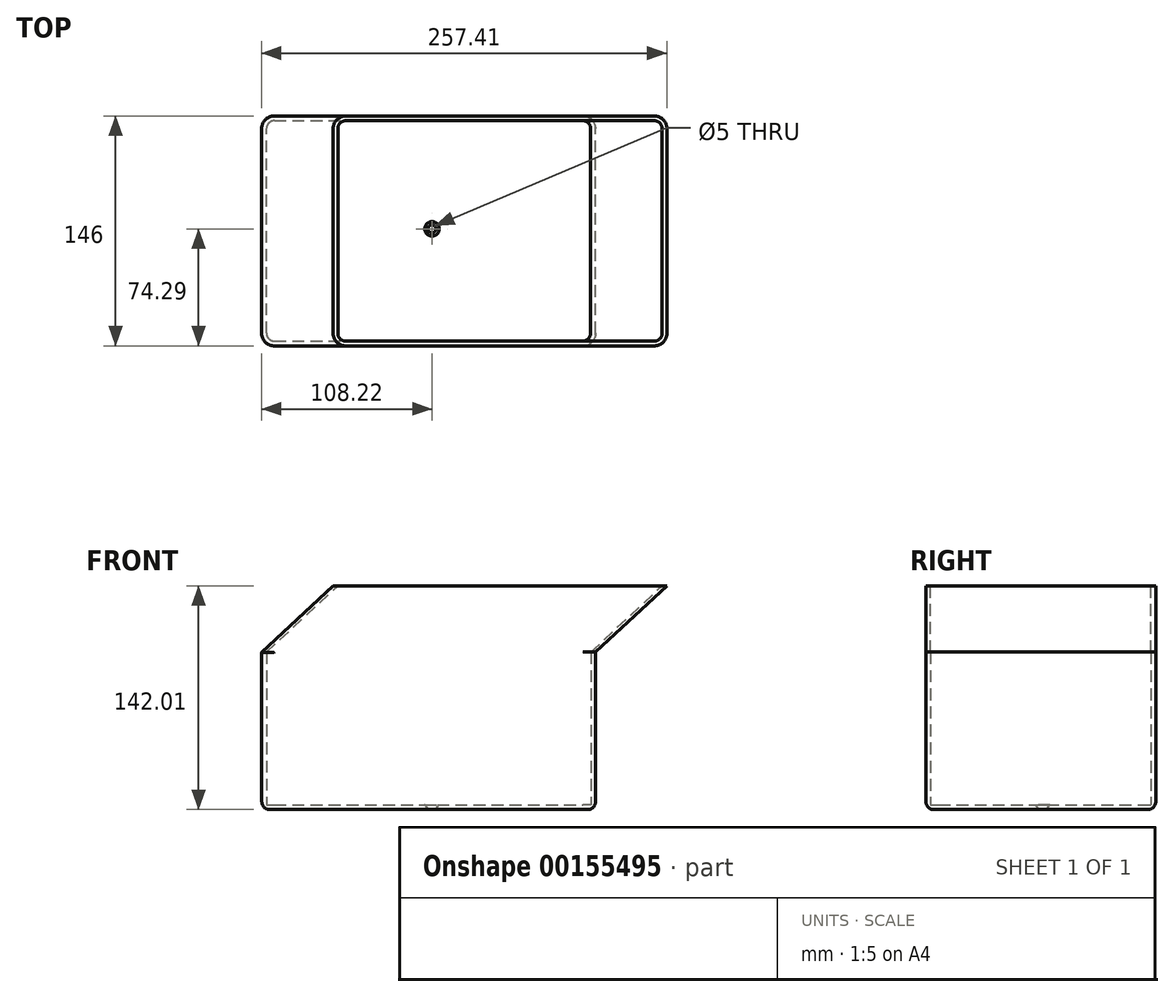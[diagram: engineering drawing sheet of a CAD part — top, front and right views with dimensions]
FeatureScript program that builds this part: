
annotation { "Feature Type Name" : "Feature", "Feature Type Description" : "" }
export const myFeature = defineFeature(function(context is Context, id is Id, definition is map)
    precondition{}
    {
        {
            var Q0;
            Q0=qCreatedBy(makeId("Top.planeOp"),FACE);
            var sketch = newSketch(context, id + "F0", { "sketchPlane" : qUnion([Q0])});
            skLineSegment(sketch, "E0.bottom", {"start": v(-100.1, -71.29) * mm, "end": v(95.9, -71.29) * mm});
            skLineSegment(sketch, "E0.top", {"start": v(-100.1, 68.71) * mm, "end": v(95.9, 68.71) * mm});
            skLineSegment(sketch, "E0.left", {"start": v(-105.1, -66.29) * mm, "end": v(-105.1, 63.71) * mm});
            skLineSegment(sketch, "E0.right", {"start": v(100.9, -66.29) * mm, "end": v(100.9, 63.71) * mm});
            skLineSegment(sketch, "E1.0", {"start": v(-100.1, 71.71) * mm, "end": v(95.9, 71.71) * mm});
            skLineSegment(sketch, "E1.1", {"start": v(-108.1, -66.29) * mm, "end": v(-108.1, 63.71) * mm});
            skLineSegment(sketch, "E1.2", {"start": v(-100.1, -74.29) * mm, "end": v(95.9, -74.29) * mm});
            skLineSegment(sketch, "E1.3", {"start": v(103.9, -66.29) * mm, "end": v(103.9, 63.71) * mm});
            skPoint(sketch, "E2.visualSharp", {"position": v(-105.1, 68.71) * mm});
            skArc(sketch, "E2.filletArc", {"start": v(-100.1, 68.71) * mm, "mid": v(-103.63, 67.25) * mm, "end": v(-105.1, 63.71) * mm});
            skPoint(sketch, "E3.visualSharp", {"position": v(100.9, 68.71) * mm});
            skArc(sketch, "E3.filletArc", {"start": v(100.9, 63.71) * mm, "mid": v(99.44, 67.25) * mm, "end": v(95.9, 68.71) * mm});
            skPoint(sketch, "E4.visualSharp", {"position": v(100.9, -71.29) * mm});
            skArc(sketch, "E4.filletArc", {"start": v(95.9, -71.29) * mm, "mid": v(99.44, -69.82) * mm, "end": v(100.9, -66.29) * mm});
            skArc(sketch, "E5.0", {"start": v(-100.1, 71.71) * mm, "mid": v(-105.75, 69.37) * mm, "end": v(-108.1, 63.71) * mm});
            skArc(sketch, "E6.0", {"start": v(103.9, 63.71) * mm, "mid": v(101.56, 69.37) * mm, "end": v(95.9, 71.71) * mm});
            skArc(sketch, "E7.0", {"start": v(95.9, -74.29) * mm, "mid": v(101.56, -71.94) * mm, "end": v(103.9, -66.29) * mm});
            skPoint(sketch, "E8.visualSharp", {"position": v(-105.1, -71.29) * mm});
            skArc(sketch, "E8.filletArc", {"start": v(-105.1, -66.29) * mm, "mid": v(-103.63, -69.82) * mm, "end": v(-100.1, -71.29) * mm});
            skArc(sketch, "E9.0", {"start": v(-108.1, -66.29) * mm, "mid": v(-105.75, -71.94) * mm, "end": v(-100.1, -74.29) * mm});
            skSolve(sketch);
        }
        {
            var Q0;
            Q0=makeQuery(id+"F0.imprint","IMPRINT",FACE,{"disambiguationData":[TD([[makeQuery(id+"F0.imprint","IMPRINT",EDGE,{"derivedFrom":sQuery(id+"F0.wireOp",EDGE,"E0.bottom")}),-1.0]])]});
            extrude(context, id + "F1", {"entities" : qUnion([Q0]), "depth" : 100 * mm});
        }
        {
            var Q0;
            Q0=makeQuery(id+"F0.imprint","IMPRINT",FACE,{"disambiguationData":[TD([[makeQuery(id+"F0.imprint","IMPRINT",EDGE,{"derivedFrom":sQuery(id+"F0.wireOp",EDGE,"E0.bottom")}),1.0]])]});
            extrude(context, id + "F2", {"entities" : qUnion([Q0]), "operationType" : NewBodyOperationType.ADD, "depth" : 3 * mm});
        }
        {
            var Q0;
            {var subQ0=sQuery(id+"F0.wireOp",EDGE,"E8.filletArc");var subQ1=sQuery(id+"F0.wireOp",EDGE,"E4.filletArc");var subQ2=sQuery(id+"F0.wireOp",EDGE,"E3.filletArc");var subQ3=sQuery(id+"F0.wireOp",EDGE,"E2.filletArc");var subQ4=sQuery(id+"F0.wireOp",EDGE,"E0.right");var subQ5=sQuery(id+"F0.wireOp",EDGE,"E0.left");var subQ6=sQuery(id+"F0.wireOp",EDGE,"E0.top");var subQ7=sQuery(id+"F0.wireOp",EDGE,"E0.bottom");Q0=makeQuery(id+"F2.boolean.opBoolean","MERGE",FACE,{"derivedFrom":[makeQuery(id+"F1.opExtrude","CAP_FACE",FACE,{"disambiguationData":[OSD([subQ7,subQ6,subQ5,subQ4,sQuery(id+"F0.wireOp",EDGE,"E1.0"),sQuery(id+"F0.wireOp",EDGE,"E1.1"),sQuery(id+"F0.wireOp",EDGE,"E1.2"),sQuery(id+"F0.wireOp",EDGE,"E1.3"),subQ3,subQ2,subQ1,sQuery(id+"F0.wireOp",EDGE,"E5.0"),sQuery(id+"F0.wireOp",EDGE,"E6.0"),sQuery(id+"F0.wireOp",EDGE,"E7.0"),subQ0,sQuery(id+"F0.wireOp",EDGE,"E9.0")])],"isStart":true}),makeQuery(id+"F2.opExtrude","CAP_FACE",FACE,{"disambiguationData":[OSD([subQ7,subQ6,subQ5,subQ4,sQuery(id+"F0.wireOp",EDGE,"eufzlCLc-SmXQ-pIzv-x4tx-eda7fgLifqMI"),subQ3,subQ2,subQ1,subQ0])],"isStart":true})]});}
            fillet(context, id + "F3", {"entities" : qUnion([Q0]), "radius" : 5 * mm, "tangentPropagation" : true, "allowEdgeOverflow" : false});
        }
        {
            var Q0;
            Q0=qCreatedBy(makeId("Front.planeOp"),FACE);
            var sketch = newSketch(context, id + "F4", { "sketchPlane" : qUnion([Q0])});
            skLineSegment(sketch, "E10.MirrorCS", {"start": v(4.6, 3) * mm, "end": v(2.5, 0.5) * mm});
            skLineSegment(sketch, "E11.MirrorCS", {"start": v(2.5, 0.5) * mm, "end": v(2.5, 0) * mm});
            skLineSegment(sketch, "E12", {"start": v(0, 6.1) * mm, "end": v(0, -1.57) * mm, "construction": true});
            skLineSegment(sketch, "E13", {"start": v(4.6, 3) * mm, "end": v(0, 3) * mm});
            skLineSegment(sketch, "E14", {"start": v(2.5, 0) * mm, "end": v(0, 0) * mm});
            skLineSegment(sketch, "E15", {"start": v(0, 0) * mm, "end": v(0, 3) * mm});
            skSolve(sketch);
        }
        {
            var Q0;
            Q0 = qSketchRegion(id + "F4", true);
            var Q1;
            Q1=sQuery(id+"F4.wireOp",EDGE,"E15");
            revolve(context, id + "F5", {"operationType" : NewBodyOperationType.REMOVE, "entities" : qUnion([Q0]), "axis" : qUnion([Q1]), "revolveType" : RevolveType.FULL});
        }
        {
            var Q0;
            Q0=makeQuery(id+"F1.opExtrude","SWEPT_FACE",FACE,{"disambiguationData":[OSD([sQuery(id+"F0.wireOp",EDGE,"E1.2")])]});
            var sketch = newSketch(context, id + "F6", { "sketchPlane" : qUnion([Q0])});
            skLineSegment(sketch, "E16", {"start": v(-105.1, 100) * mm, "end": v(-108.1, 100) * mm});
            skLineSegment(sketch, "E17", {"start": v(-108.1, 100) * mm, "end": v(-100.31, 106.98) * mm});
            skLineSegment(sketch, "E18", {"start": v(-105.1, 100) * mm, "end": v(-98.12, 106.25) * mm});
            skPoint(sketch, "E19.orphan", {"position": v(-100.1, 100) * mm});
            skLineSegment(sketch, "E20", {"start": v(-100.31, 106.98) * mm, "end": v(-98.4, 106.98) * mm});
            skArc(sketch, "E21.filletArc", {"start": v(-98.12, 106.25) * mm, "mid": v(-98.01, 106.71) * mm, "end": v(-98.4, 106.98) * mm});
            skSolve(sketch);
        }
        {
            var Q0;
            Q0=makeQuery(id+"F1.opExtrude","CAP_FACE",FACE,{"disambiguationData":[OSD([sQuery(id+"F0.wireOp",EDGE,"E0.bottom"),sQuery(id+"F0.wireOp",EDGE,"E0.top"),sQuery(id+"F0.wireOp",EDGE,"E0.left"),sQuery(id+"F0.wireOp",EDGE,"E0.right"),sQuery(id+"F0.wireOp",EDGE,"E1.0"),sQuery(id+"F0.wireOp",EDGE,"E1.1"),sQuery(id+"F0.wireOp",EDGE,"E1.2"),sQuery(id+"F0.wireOp",EDGE,"E1.3"),sQuery(id+"F0.wireOp",EDGE,"E2.filletArc"),sQuery(id+"F0.wireOp",EDGE,"E3.filletArc"),sQuery(id+"F0.wireOp",EDGE,"E4.filletArc"),sQuery(id+"F0.wireOp",EDGE,"E5.0"),sQuery(id+"F0.wireOp",EDGE,"E6.0"),sQuery(id+"F0.wireOp",EDGE,"E7.0"),sQuery(id+"F0.wireOp",EDGE,"E8.filletArc"),sQuery(id+"F0.wireOp",EDGE,"E9.0")])],"isStart":false});
            var sketch = newSketch(context, id + "F7", { "sketchPlane" : qUnion([Q0])});
            skLineSegment(sketch, "E22", {"start": v(-70, 45) * mm, "end": v(70, 45) * mm});
            skLineSegment(sketch, "E23", {"start": v(-75, 40) * mm, "end": v(-75, -40) * mm});
            skLineSegment(sketch, "E24.MirrorCS", {"start": v(75, 40) * mm, "end": v(75, -40) * mm});
            skLineSegment(sketch, "E25.MirrorCS", {"start": v(-70, -45) * mm, "end": v(70, -45) * mm});
            skPoint(sketch, "E26.newPointA", {"position": v(-75, 52.38) * mm});
            skPoint(sketch, "E26.newPointB", {"position": v(-77.7, 45) * mm});
            skArc(sketch, "E26.filletArc", {"start": v(-70, 45) * mm, "mid": v(-73.54, 43.54) * mm, "end": v(-75, 40) * mm});
            skPoint(sketch, "E27.newPointA", {"position": v(-75, -51.15) * mm});
            skPoint(sketch, "E27.newPointB", {"position": v(-77.7, -45) * mm});
            skArc(sketch, "E27.filletArc", {"start": v(-75, -40) * mm, "mid": v(-73.54, -43.54) * mm, "end": v(-70, -45) * mm});
            skPoint(sketch, "E28.newPointA", {"position": v(82.32, -45) * mm});
            skPoint(sketch, "E28.newPointB", {"position": v(75, -51.15) * mm});
            skArc(sketch, "E28.filletArc", {"start": v(70, -45) * mm, "mid": v(73.54, -43.54) * mm, "end": v(75, -40) * mm});
            skPoint(sketch, "E29.newPointA", {"position": v(82.32, 45) * mm});
            skPoint(sketch, "E29.newPointB", {"position": v(75, 52.38) * mm});
            skArc(sketch, "E29.filletArc", {"start": v(75, 40) * mm, "mid": v(73.54, 43.54) * mm, "end": v(70, 45) * mm});
            skLineSegment(sketch, "E30.0", {"start": v(-70, 50) * mm, "end": v(70, 50) * mm});
            skArc(sketch, "E30.1", {"start": v(-70, 50) * mm, "mid": v(-77.07, 47.07) * mm, "end": v(-80, 40) * mm});
            skLineSegment(sketch, "E30.2", {"start": v(-80, 40) * mm, "end": v(-80, -40) * mm});
            skLineSegment(sketch, "E30.3", {"start": v(80, 40) * mm, "end": v(80, -40) * mm});
            skArc(sketch, "E30.4", {"start": v(70, -50) * mm, "mid": v(77.07, -47.07) * mm, "end": v(80, -40) * mm});
            skLineSegment(sketch, "E30.5", {"start": v(-70, -50) * mm, "end": v(70, -50) * mm});
            skArc(sketch, "E30.6", {"start": v(-80, -40) * mm, "mid": v(-77.07, -47.07) * mm, "end": v(-70, -50) * mm});
            skArc(sketch, "E31.0", {"start": v(80, 40) * mm, "mid": v(77.07, 47.07) * mm, "end": v(70, 50) * mm});
            skLineSegment(sketch, "E32.0", {"start": v(-110.1, 63.71) * mm, "end": v(-110.1, -66.29) * mm});
            skArc(sketch, "E32.1", {"start": v(-100.1, 73.71) * mm, "mid": v(-107.17, 70.78) * mm, "end": v(-110.1, 63.71) * mm});
            skArc(sketch, "E32.2", {"start": v(-110.1, -66.29) * mm, "mid": v(-107.17, -73.36) * mm, "end": v(-100.1, -76.29) * mm});
            skLineSegment(sketch, "E32.3", {"start": v(95.9, 73.71) * mm, "end": v(-100.1, 73.71) * mm});
            skLineSegment(sketch, "E32.4", {"start": v(-100.1, -76.29) * mm, "end": v(95.9, -76.29) * mm});
            skArc(sketch, "E32.5", {"start": v(95.9, -76.29) * mm, "mid": v(102.98, -73.36) * mm, "end": v(105.9, -66.29) * mm});
            skLineSegment(sketch, "E32.6", {"start": v(105.9, -66.29) * mm, "end": v(105.9, 63.71) * mm});
            skArc(sketch, "E32.7", {"start": v(105.9, 63.71) * mm, "mid": v(102.98, 70.78) * mm, "end": v(95.9, 73.71) * mm});
            skSolve(sketch);
        }
        {
            var Q0;
            Q0=makeQuery(id+"F7.imprint","IMPRINT",FACE,{"disambiguationData":[TD([[makeQuery(id+"F7.imprint","IMPRINT",EDGE,{"derivedFrom":sQuery(id+"F7.wireOp",EDGE,"E22")}),1.0]])]});
            extrude(context, id + "F8", {"entities" : qUnion([Q0]), "depth" : 30 * mm, "hasSecondDirection" : true, "secondDirectionOppositeDirection" : false, "secondDirectionDepth" : 25 * mm});
        }
        {
            var Q0;
            {var subQ0=sQuery(id+"F0.wireOp",EDGE,"E1.2");Q0=makeQuery(id+"F6.imprint","IMPRINT",FACE,{"disambiguationData":[TD([[makeQuery(id+"F6.imprint","IMPRINT",EDGE,{"derivedFrom":makeQuery(id+"F1.opExtrude","CAP_EDGE",EDGE,{"disambiguationData":[OSD([subQ0])],"isStart":false})}),-1.0]])]});}
            var sketch = newSketch(context, id + "F9", { "sketchPlane" : qUnion([Q0])});
            skLineSegment(sketch, "E33", {"start": v(-99.7, 99.89) * mm, "end": v(-54.3, 142.01) * mm});
            skSolve(sketch);
        }
        {
            var Q0;
            Q0=makeQuery(id+"F8.opExtrude","SWEPT_BODY",BODY,{"disambiguationData":[OSD([sQuery(id+"F7.wireOp",EDGE,"E22"),sQuery(id+"F7.wireOp",EDGE,"E23"),sQuery(id+"F7.wireOp",EDGE,"E24.MirrorCS"),sQuery(id+"F7.wireOp",EDGE,"E25.MirrorCS"),sQuery(id+"F7.wireOp",EDGE,"E26.filletArc"),sQuery(id+"F7.wireOp",EDGE,"E27.filletArc"),sQuery(id+"F7.wireOp",EDGE,"E28.filletArc"),sQuery(id+"F7.wireOp",EDGE,"E29.filletArc"),sQuery(id+"F7.wireOp",EDGE,"E30.0"),sQuery(id+"F7.wireOp",EDGE,"E30.1"),sQuery(id+"F7.wireOp",EDGE,"E30.2"),sQuery(id+"F7.wireOp",EDGE,"E30.3"),sQuery(id+"F7.wireOp",EDGE,"E30.4"),sQuery(id+"F7.wireOp",EDGE,"E30.5"),sQuery(id+"F7.wireOp",EDGE,"E30.6"),sQuery(id+"F7.wireOp",EDGE,"E31.0")])]});
            deleteBodies(context, id + "F10", {"entities" : qUnion([Q0])});
        }
        {
            var Q0;
            Q0=makeQuery(id+"F7.imprint","IMPRINT",FACE,{"disambiguationData":[TD([[makeQuery(id+"F7.imprint","IMPRINT",EDGE,{"derivedFrom":makeQuery(id+"F1.opExtrude","CAP_EDGE",EDGE,{"disambiguationData":[OSD([sQuery(id+"F0.wireOp",EDGE,"E0.bottom")])],"isStart":false})}),-1.0]])]});
            var Q1;
            Q1=sQuery(id+"F9.wireOp",EDGE,"E33");
            sweep(context, id + "F11", {"operationType" : NewBodyOperationType.ADD, "profiles" : qUnion([Q0]), "path" : qUnion([Q1])});
        }
    });
